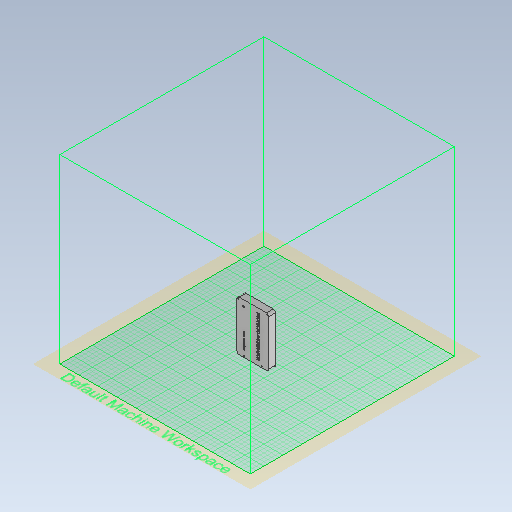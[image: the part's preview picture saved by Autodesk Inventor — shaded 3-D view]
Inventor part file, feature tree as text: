
AUTODESK INVENTOR PART (.ipt)
format: ipt  version: 2020 (Build 240168000, 168)  size: 1,750,016 bytes
history: native  units: mm
features: sketch x7, extrude x3, hole x2, emboss x2, fillet x1
ambient origin geometry x8: Origin, YZ Plane, XZ Plane, XY Plane, X Axis, Y Axis, Z Axis, Center Point
bodies: Solid1 (feature_tree)
feature tree (15):
  sketch  "Sketch1"  dims[d0=70.0mm d1=110.0mm]
  extrude  "Extrusion1"  Depth=110.0mm
  extrude  "Extrusion2"  Depth=100.0mm
  fillet  "Fillet1"  Radius=15.0mm
  extrude  "Extrusion3"  Depth=5.0mm
  hole  "Hole1"  [1 undecoded]
  hole  "Hole2"  [1 undecoded]
  emboss  "Emboss1"
  emboss  "Emboss2"
  sketch  "Sketch8"  dims[d15=2.5mm d16=1.5mm d17=6.0mm d18=2.5mm d19=1.0mm d20=14.3117mm d21=40.0mm d22=20.594885mm d23=20.0mm d24=0.0mm d25=20.0mm d26=180.0deg d27=1.5mm d28=6.0mm d29=2.5mm d30=1.0mm d31=14.3117mm d32=40.0mm d33=20.594885mm d34=1.0mm d35=0.0mm d46=0.5mm d47=0.0mm]
  sketch  "Sketch2"  dims[d2=60.0mm d3=100.0mm d4=15.0mm d5=0.0mm]
  sketch  "Sketch3"  dims[d6=5.0mm d7=0.0mm d8=5.0mm]
  sketch  "Sketch4"  dims[d9=60.0mm d10=4.0mm]
  sketch  "Sketch5"  dims[d11=5.0mm d12=0.0mm d13=2.5mm]
  sketch  "Sketch7"  dims[d14=135.0deg]
note: 2 required parameter values undecoded (feature->parameter linkage not recoverable at this tier; creation-order binding heuristic only, values carry confidence <= 0.55)
